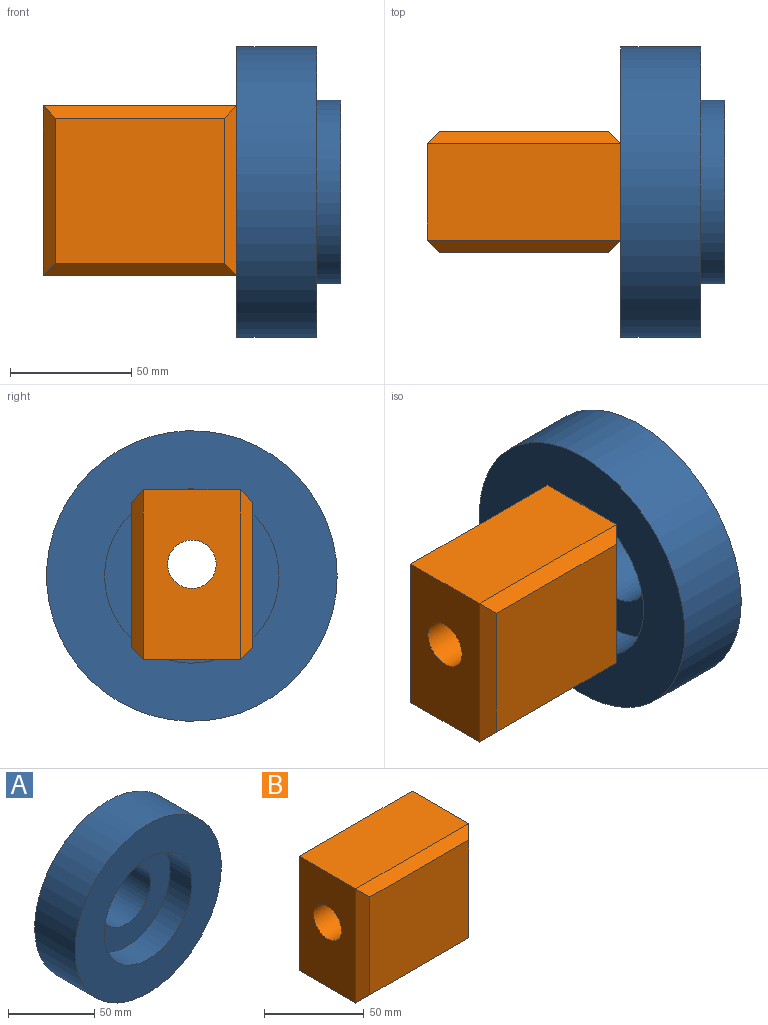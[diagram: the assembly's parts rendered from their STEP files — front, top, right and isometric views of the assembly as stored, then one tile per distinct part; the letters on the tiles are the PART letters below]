
ASSEMBLY  parts=2 mates=1
PART A: 8 faces, bbox 120x43x120 mm
  f0: cylinder r=20mm len=40mm, axis (0,1,0), area 3141.6mm2, adj f1,f7
  f1: plane 76x76mm, normal (0,1,0), area 3279.8mm2, adj f0,f2
  f2: cylinder r=38mm len=76mm, axis (0,1,0), area 2387.6mm2, adj f1,f3
  f3: plane 120x120mm, normal (0,1,0), area 6773.3mm2, adj f2,f4
  f4: cylinder r=60mm len=120mm, axis (0,1,0), area 12440.7mm2, adj f3,f5
  f5: plane 120x120mm, normal (0,-1,0), area 7238.2mm2, adj f4,f6
  f6: cylinder r=36mm len=72mm, axis (0,1,0), area 4071.5mm2, adj f5,f7
  f7: plane 72x72mm, normal (0,-1,0), area 2814.9mm2, adj f0,f6
PART B: 15 faces, bbox 80x50x70 mm
  f0: plane 70x40mm, normal (1,0,0), area 2485.8mm2, adj f4,f5,f6,f8,f12
  f1: plane 70x60mm, normal (0,1,0), area 4200mm2, adj f11,f12,f13,f14
  f2: plane 70x40mm, normal (-1,0,0), area 2485.8mm2, adj f4,f5,f6,f9,f13
  f3: plane 70x60mm, normal (0,-1,0), area 4200mm2, adj f7,f8,f9,f10
  f4: plane 80x40mm, normal (0,0,1), area 3200mm2, adj f0,f2,f10,f14
  f5: plane 80x40mm, normal (0,0,-1), area 3200mm2, adj f0,f2,f7,f11
  f6: cylinder r=10mm len=80mm, axis (1,0,0), area 5026.5mm2, adj f0,f2
  f7: plane 80x5mm, normal (0,-0.71,-0.71), area 530.3mm2, adj f3,f5,f8,f9
  f8: plane 70x5mm, normal (0.71,-0.71,0), area 459.6mm2, adj f0,f3,f7,f10
  f9: plane 70x5mm, normal (-0.71,-0.71,0), area 459.6mm2, adj f2,f3,f7,f10
  f10: plane 80x5mm, normal (0,-0.71,0.71), area 530.3mm2, adj f3,f4,f8,f9
  f11: plane 80x5mm, normal (0,0.71,-0.71), area 530.3mm2, adj f1,f5,f12,f13
  f12: plane 70x5mm, normal (0.71,0.71,0), area 459.6mm2, adj f0,f1,f11,f14
  f13: plane 70x5mm, normal (-0.71,0.71,0), area 459.6mm2, adj f1,f2,f11,f14
  f14: plane 80x5mm, normal (0,0.71,0.71), area 530.3mm2, adj f1,f4,f12,f13
PLACE A rot(axis=(0.58,0.58,-0.58),120deg) t=(135.29,-35.72,6.47)mm
PLACE B t=(9.96,8.78,-27.98)mm
MATE revolute A.f0 <-> B.f0  axis (-1,0,0) through (49.96,8.78,6.47)mm
